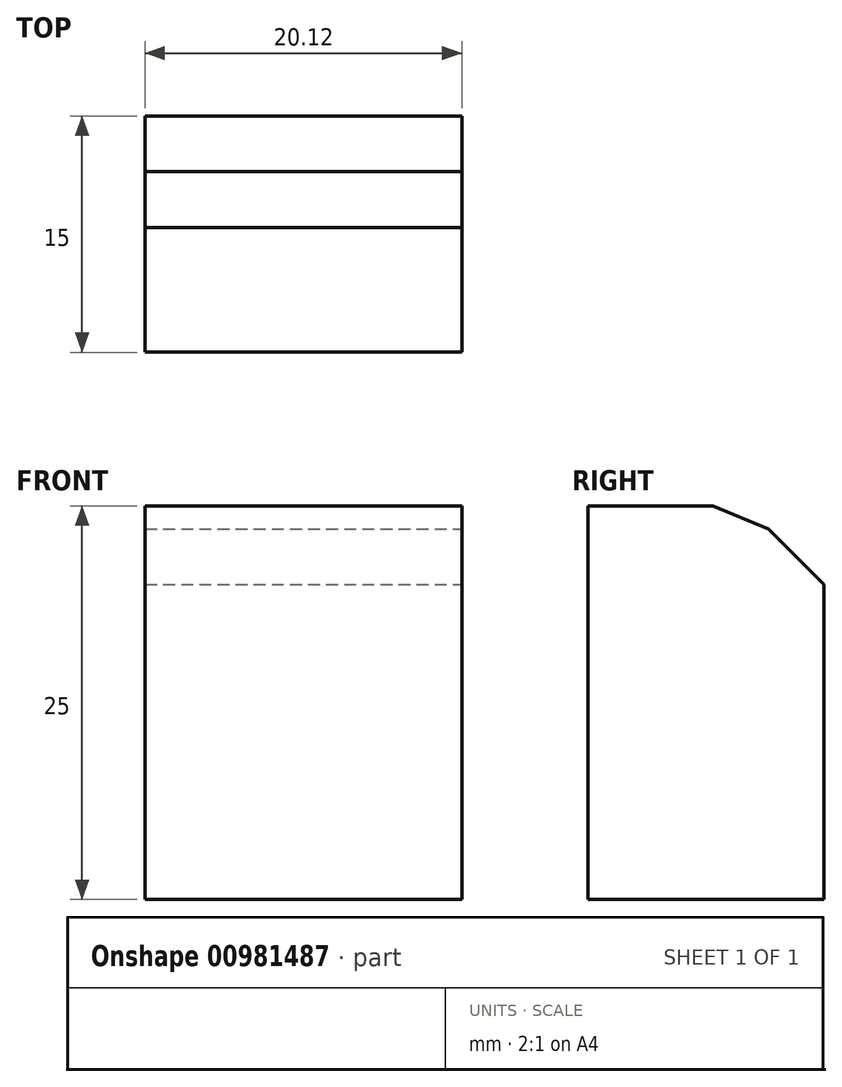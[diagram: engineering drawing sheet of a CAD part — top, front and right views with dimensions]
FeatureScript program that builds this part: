
annotation { "Feature Type Name" : "Feature", "Feature Type Description" : "" }
export const myFeature = defineFeature(function(context is Context, id is Id, definition is map)
    precondition{}
    {
        {
            var Q0;
            Q0=qCreatedBy(makeId("Top.planeOp"),FACE);
            var sketch = newSketch(context, id + "F0", { "sketchPlane" : qUnion([Q0])});
            skLineSegment(sketch, "E0", {"start": v(0, 11.07) * mm, "end": v(-20.12, 11.07) * mm});
            skLineSegment(sketch, "E1", {"start": v(-20.12, 11.07) * mm, "end": v(-20.12, -3.93) * mm});
            skLineSegment(sketch, "E2", {"start": v(-20.12, -3.93) * mm, "end": v(0, -3.93) * mm});
            skLineSegment(sketch, "E3", {"start": v(0, -3.93) * mm, "end": v(0, 11.07) * mm});
            skSolve(sketch);
        }
        {
            var Q0;
            Q0=makeQuery(id+"F0.imprint","IMPRINT",FACE,{"disambiguationData":[TD([[makeQuery(id+"F0.imprint","IMPRINT",EDGE,{"derivedFrom":sQuery(id+"F0.wireOp",EDGE,"E0")}),1.0]])]});
            extrude(context, id + "F1", {"entities" : qUnion([Q0]), "depth" : 25 * mm, "offsetDistance" : 25 * mm});
        }
        {
            var Q0;
            Q0=makeQuery(id+"F1.opExtrude","CAP_EDGE",EDGE,{"disambiguationData":[OSD([sQuery(id+"F0.wireOp",EDGE,"E0")])],"isStart":false});
            chamfer(context, id + "F2", {"entities" : qUnion([Q0]), "width" : 5 * mm, "tangentPropagation" : true});
        }
        {
            var Q0;
            {var subQ0=sQuery(id+"F0.wireOp",EDGE,"E0");Q0=makeQuery(id+"F2.opChamfer","BLEND_EDGE",EDGE,{"blendedFrom":[makeQuery(id+"F1.opExtrude","CAP_EDGE",EDGE,{"disambiguationData":[OSD([subQ0])],"isStart":false}),makeQuery(id+"F1.opExtrude","CAP_FACE",FACE,{"disambiguationData":[OSD([subQ0,sQuery(id+"F0.wireOp",EDGE,"E1"),sQuery(id+"F0.wireOp",EDGE,"E2"),sQuery(id+"F0.wireOp",EDGE,"E3")])],"isStart":false})],"blendedInto":[makeQuery(id+"F1.opExtrude","CAP_FACE",FACE,{"disambiguationData":[OSD([subQ0,sQuery(id+"F0.wireOp",EDGE,"E1"),sQuery(id+"F0.wireOp",EDGE,"E2"),sQuery(id+"F0.wireOp",EDGE,"E3")])],"isStart":false})]});}
            chamfer(context, id + "F3", {"entities" : qUnion([Q0]), "width" : 5 * mm, "tangentPropagation" : true});
        }
    });
